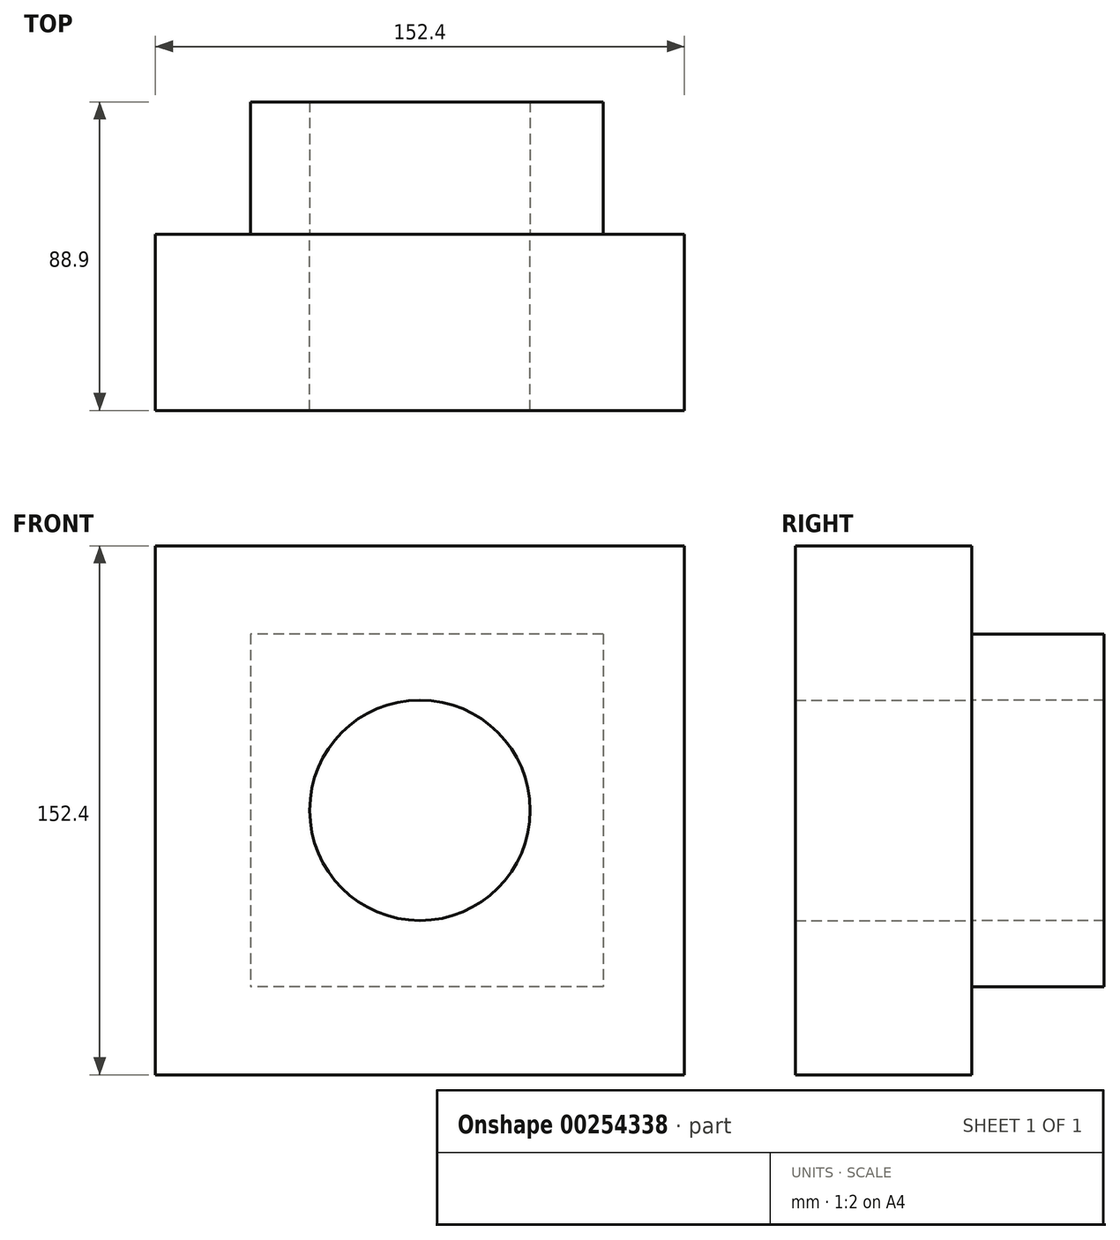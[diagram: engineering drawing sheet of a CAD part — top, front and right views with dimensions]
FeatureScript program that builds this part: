
annotation { "Feature Type Name" : "Feature", "Feature Type Description" : "" }
export const myFeature = defineFeature(function(context is Context, id is Id, definition is map)
    precondition{}
    {
        {
            var Q0;
            Q0=qCreatedBy(makeId("Front.planeOp"),FACE);
            var sketch = newSketch(context, id + "F0", { "sketchPlane" : qUnion([Q0])});
            skCircle(sketch, "E0", {"center": v(0, 0) * mm, "radius": 31.75 * mm});
            skLineSegment(sketch, "E1.bottom", {"start": v(52.8, 50.8) * mm, "end": v(-48.8, 50.8) * mm});
            skLineSegment(sketch, "E1.top", {"start": v(52.8, -50.8) * mm, "end": v(-48.8, -50.8) * mm});
            skLineSegment(sketch, "E1.left", {"start": v(52.8, 50.8) * mm, "end": v(52.8, -50.8) * mm});
            skLineSegment(sketch, "E1.right", {"start": v(-48.8, 50.8) * mm, "end": v(-48.8, -50.8) * mm});
            skPoint(sketch, "E1.middle", {"position": v(2, 0) * mm});
            skLineSegment(sketch, "E2.bottom", {"start": v(76.2, 76.2) * mm, "end": v(-76.2, 76.2) * mm});
            skLineSegment(sketch, "E2.top", {"start": v(76.2, -76.2) * mm, "end": v(-76.2, -76.2) * mm});
            skLineSegment(sketch, "E2.left", {"start": v(76.2, 76.2) * mm, "end": v(76.2, -76.2) * mm});
            skLineSegment(sketch, "E2.right", {"start": v(-76.2, 76.2) * mm, "end": v(-76.2, -76.2) * mm});
            skSolve(sketch);
        }
        {
            var Q0;
            Q0=makeQuery(id+"F0.imprint","IMPRINT",FACE,{"disambiguationData":[TD([[makeQuery(id+"F0.imprint","IMPRINT",EDGE,{"derivedFrom":sQuery(id+"F0.wireOp",EDGE,"E0")}),-1.0]])]});
            extrude(context, id + "F1", {"entities" : qUnion([Q0]), "oppositeDirection" : true, "depth" : 38.1 * mm});
        }
        {
            var Q0;
            Q0=makeQuery(id+"F0.imprint","IMPRINT",FACE,{"disambiguationData":[TD([[makeQuery(id+"F0.imprint","IMPRINT",EDGE,{"derivedFrom":sQuery(id+"F0.wireOp",EDGE,"E1.bottom")}),-1.0]])]});
            var Q1;
            Q1=makeQuery(id+"F0.imprint","IMPRINT",FACE,{"disambiguationData":[TD([[makeQuery(id+"F0.imprint","IMPRINT",EDGE,{"derivedFrom":sQuery(id+"F0.wireOp",EDGE,"E0")}),-1.0]])]});
            extrude(context, id + "F2", {"entities" : qUnion([Q0, Q1]), "depth" : 50.8 * mm});
        }
    });
